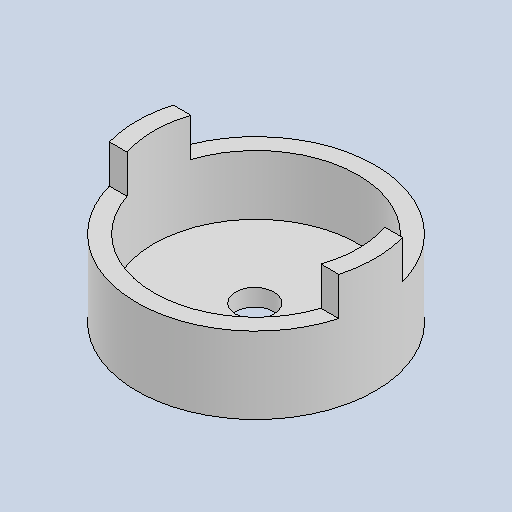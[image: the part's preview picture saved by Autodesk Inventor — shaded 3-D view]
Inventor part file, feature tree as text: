
AUTODESK INVENTOR PART (.ipt)
format: ipt  version: 2022 (Build 260153000, 153)  size: 126,976 bytes
history: native  units: mm
features: sketch x4, extrude x3, hole x1
ambient origin geometry x8: Origin, YZ Plane, XZ Plane, XY Plane, X Axis, Y Axis, Z Axis, Center Point
bodies: Solid1 (feature_tree)
feature tree (8):
  extrude  "Extrusion1"  Depth=24.0mm
  sketch  "Sketch2"  dims[d2=7.0mm d3=0.0mm d4=28.0mm]
  extrude  "Extrusion3"  Depth=7.0mm
  hole  "Hole2"  [1 undecoded]
  extrude  "Extrusion4"  Depth=4.5mm TaperAngle=0.0deg
  sketch  "Sketch1"  dims[d0=28.0mm d1=24.0mm]
  sketch  "Sketch3"  dims[d5=7.5mm d8=2.0mm d9=0.0mm]
  sketch  "Sketch5"  dims[d17=28.0mm d18=4.5mm d19=6.0mm d20=10.59mm d21=3.0mm d22=90.0deg d23=8.0mm d24=20.594885mm d25=4.5mm d26=0.0mm d27=24.0mm d28=28.0mm]
note: 1 required parameter value undecoded (feature->parameter linkage not recoverable at this tier; creation-order binding heuristic only, values carry confidence <= 0.55)
